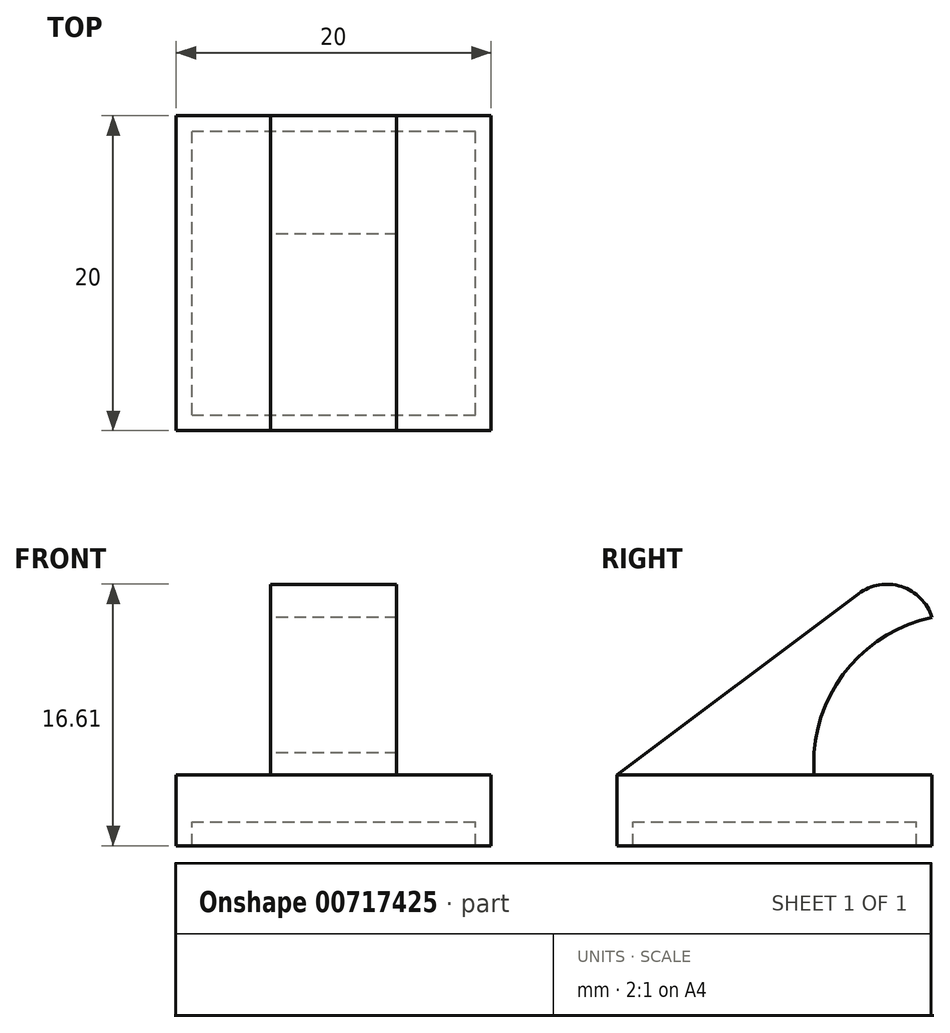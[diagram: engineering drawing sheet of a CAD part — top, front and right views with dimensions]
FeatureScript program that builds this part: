
annotation { "Feature Type Name" : "Feature", "Feature Type Description" : "" }
export const myFeature = defineFeature(function(context is Context, id is Id, definition is map)
    precondition{}
    {
        {
            var Q0;
            Q0=qCreatedBy(makeId("Right.planeOp"),FACE);
            var sketch = newSketch(context, id + "F0", { "sketchPlane" : qUnion([Q0])});
            skLineSegment(sketch, "E0", {"start": v(-18.18, 4.96) * mm, "end": v(1.82, 4.96) * mm});
            skLineSegment(sketch, "E1", {"start": v(-18.18, 4.96) * mm, "end": v(-18.18, 7.96) * mm});
            skLineSegment(sketch, "E2", {"start": v(1.82, 4.96) * mm, "end": v(1.82, 7.96) * mm});
            skLineSegment(sketch, "E3", {"start": v(-5.68, 7.96) * mm, "end": v(1.82, 7.96) * mm});
            skLineSegment(sketch, "E4", {"start": v(-18.18, 7.96) * mm, "end": v(1.82, 22.96) * mm});
            skLineSegment(sketch, "E5", {"start": v(1.82, 22.96) * mm, "end": v(1.82, 17.96) * mm});
            skPoint(sketch, "E6", {"position": v(1.82, 12.96) * mm});
            skPoint(sketch, "E7", {"position": v(1.82, 17.96) * mm});
            skLineSegment(sketch, "E8", {"start": v(-5.68, 7.96) * mm, "end": v(-5.68, 9.36) * mm});
            skPoint(sketch, "E9", {"position": v(-4.32, 13.6) * mm});
            skArc(sketch, "E10", {"start": v(1.82, 17.96) * mm, "mid": v(-3.36, 14.91) * mm, "end": v(-5.68, 9.36) * mm});
            skArc(sketch, "E11.trimOffspring", {"start": v(1.82, 17.96) * mm, "mid": v(-1.7, 16.42) * mm, "end": v(-4.32, 13.6) * mm});
            skSolve(sketch);
        }
        {
            var Q0;
            Q0 = qSketchRegion(id + "F0", true);
            extrude(context, id + "F1", {"entities" : qUnion([Q0]), "depth" : 20 * mm, "offsetDistance" : 25 * mm});
        }
        {
            var Q0;
            Q0=makeQuery(id+"F1.opExtrude","SWEPT_FACE",FACE,{"disambiguationData":[OSD([sQuery(id+"F0.wireOp",EDGE,"E5")])]});
            var sketch = newSketch(context, id + "F2", { "sketchPlane" : qUnion([Q0])});
            skLineSegment(sketch, "E12", {"start": v(-20, 22.96) * mm, "end": v(-20, 7.96) * mm});
            skLineSegment(sketch, "E13", {"start": v(-20, 22.96) * mm, "end": v(-14, 22.96) * mm});
            skLineSegment(sketch, "E14", {"start": v(-14, 22.96) * mm, "end": v(-14, 7.96) * mm});
            skLineSegment(sketch, "E15", {"start": v(-14, 7.96) * mm, "end": v(-20, 7.96) * mm});
            skLineSegment(sketch, "E16", {"start": v(0, 22.96) * mm, "end": v(0, 7.96) * mm});
            skPoint(sketch, "E16.endSnap0", {"position": v(0, 20.46) * mm});
            skLineSegment(sketch, "E17", {"start": v(0, 22.96) * mm, "end": v(-6, 22.96) * mm});
            skLineSegment(sketch, "E18", {"start": v(-6, 22.96) * mm, "end": v(-6, 7.96) * mm});
            skLineSegment(sketch, "E19", {"start": v(-6, 7.96) * mm, "end": v(0, 7.96) * mm});
            skSolve(sketch);
        }
        {
            var Q0;
            Q0 = qSketchRegion(id + "F2", true);
            extrude(context, id + "F3", {"entities" : qUnion([Q0]), "operationType" : NewBodyOperationType.REMOVE, "endBound" : BoundingType.THROUGH_ALL, "oppositeDirection" : true, "depth" : 25 * mm, "offsetDistance" : 25 * mm});
        }
        {
            var Q0;
            Q0=makeQuery(id+"F1.opExtrude","SWEPT_EDGE",EDGE,{"disambiguationData":[OSD([sQuery(id+"F0.wireOp",EDGE,"E4"),sQuery(id+"F0.wireOp",EDGE,"E5")])]});
            fillet(context, id + "F4", {"entities" : qUnion([Q0]), "radius" : 3 * mm, "tangentPropagation" : true, "allowEdgeOverflow" : false});
        }
        {
            var Q0;
            Q0=makeQuery(id+"F1.opExtrude","SWEPT_FACE",FACE,{"disambiguationData":[OSD([sQuery(id+"F0.wireOp",EDGE,"E0")])]});
            var sketch = newSketch(context, id + "F5", { "sketchPlane" : qUnion([Q0])});
            skLineSegment(sketch, "E20", {"start": v(0, 18.18) * mm, "end": v(20, 18.18) * mm});
            skLineSegment(sketch, "E21", {"start": v(20, 18.18) * mm, "end": v(20, -1.82) * mm});
            skLineSegment(sketch, "E22", {"start": v(20, -1.82) * mm, "end": v(0, -1.82) * mm});
            skLineSegment(sketch, "E23", {"start": v(0, -1.82) * mm, "end": v(0, 18.18) * mm});
            skLineSegment(sketch, "E24.trimOffspring", {"start": v(1, 17.18) * mm, "end": v(19, 17.18) * mm});
            skLineSegment(sketch, "E25.trimOffspring", {"start": v(1, 17.18) * mm, "end": v(1, -0.82) * mm});
            skLineSegment(sketch, "E26.trimOffspring", {"start": v(19, 17.18) * mm, "end": v(19, -0.82) * mm});
            skLineSegment(sketch, "E27", {"start": v(19, -0.82) * mm, "end": v(1, -0.82) * mm});
            skSolve(sketch);
        }
        {
            var Q0;
            Q0=makeQuery(id+"F5.imprint","IMPRINT",FACE,{"disambiguationData":[TD([[makeQuery(id+"F5.imprint","IMPRINT",EDGE,{"derivedFrom":sQuery(id+"F5.wireOp",EDGE,"E20")}),1.0]])]});
            extrude(context, id + "F6", {"entities" : qUnion([Q0]), "operationType" : NewBodyOperationType.ADD, "depth" : 1.5 * mm, "offsetDistance" : 25 * mm});
        }
    });
